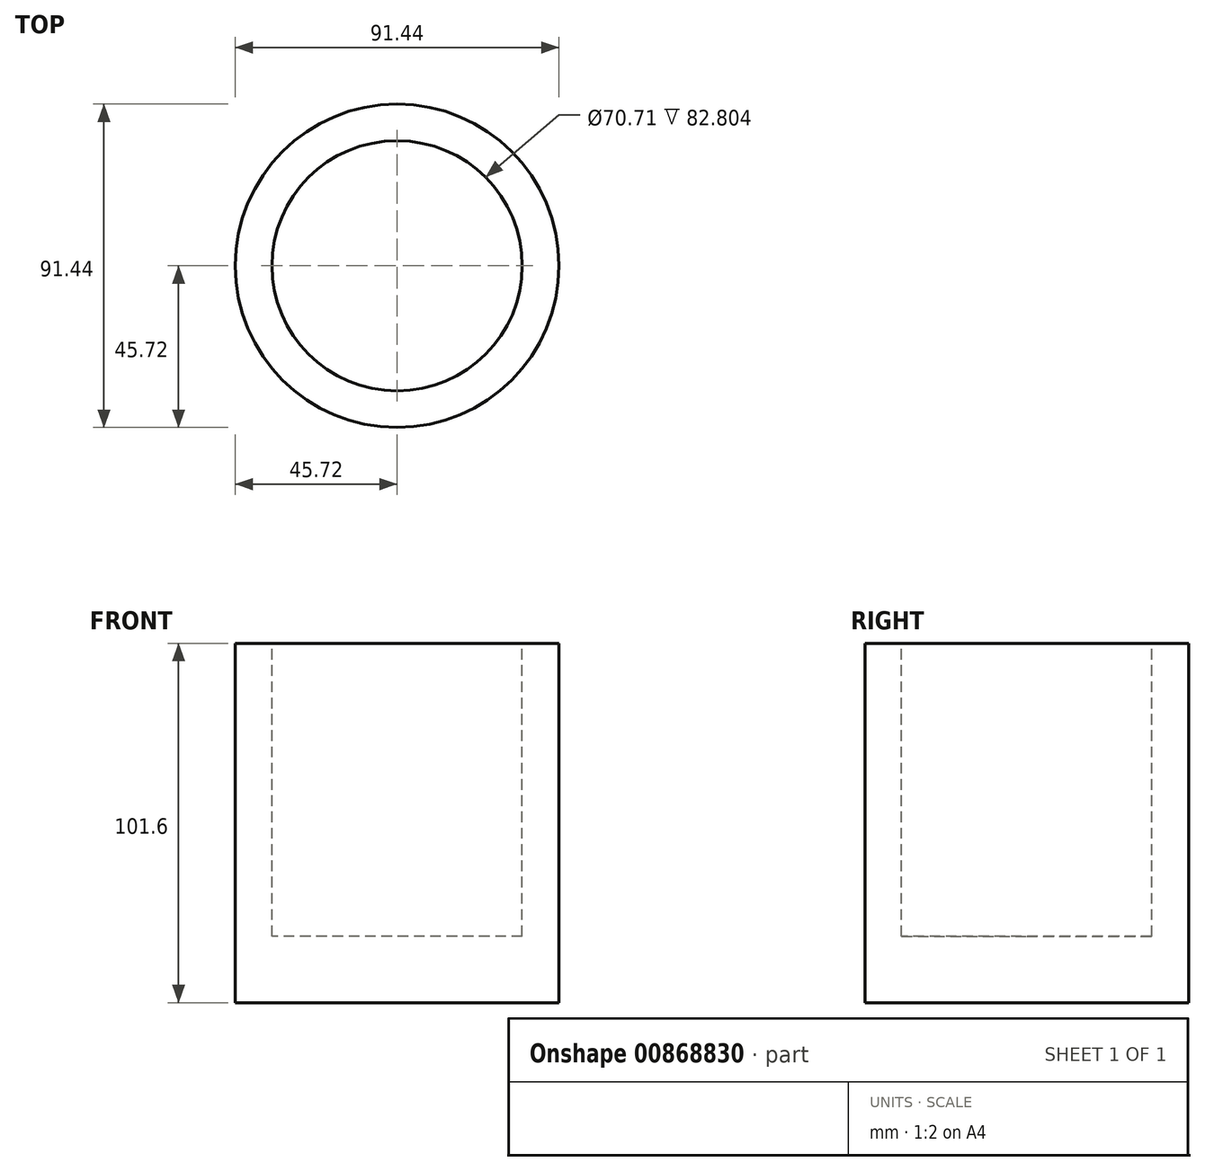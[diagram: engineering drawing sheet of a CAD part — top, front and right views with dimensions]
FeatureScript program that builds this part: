
annotation { "Feature Type Name" : "Feature", "Feature Type Description" : "" }
export const myFeature = defineFeature(function(context is Context, id is Id, definition is map)
    precondition{}
    {
        {
            var Q0;
            Q0=qCreatedBy(makeId("Top.planeOp"),FACE);
            var sketch = newSketch(context, id + "F0", { "sketchPlane" : qUnion([Q0])});
            skCircle(sketch, "E0", {"center": v(0, 0) * mm, "radius": 45.72 * mm});
            skPoint(sketch, "E0.first.point", {"position": v(-32.88, 31.77) * mm});
            skPoint(sketch, "E0.second.point", {"position": v(32.45, -32.21) * mm});
            skPoint(sketch, "E0.third.point", {"position": v(21.79, 40.2) * mm});
            skSolve(sketch);
        }
        {
            var Q0;
            Q0=makeQuery(id+"F0.imprint","IMPRINT",FACE,{"disambiguationData":[TD([[makeQuery(id+"F0.imprint","IMPRINT",EDGE,{"derivedFrom":sQuery(id+"F0.wireOp",EDGE,"E0")}),1.0]])]});
            extrude(context, id + "F1", {"entities" : qUnion([Q0]), "depth" : 101.6 * mm, "offsetDistance" : 25.4 * mm});
        }
        {
            var Q0;
            Q0=makeQuery(id+"F1.opExtrude","CAP_FACE",FACE,{"disambiguationData":[OSD([sQuery(id+"F0.wireOp",EDGE,"E0")])],"isStart":false});
            var sketch = newSketch(context, id + "F2", { "sketchPlane" : qUnion([Q0])});
            skCircle(sketch, "E1", {"center": v(0, 0) * mm, "radius": 35.35 * mm});
            skSolve(sketch);
        }
        {
            var Q0;
            Q0=makeQuery(id+"F2.imprint","IMPRINT",FACE,{"disambiguationData":[TD([[makeQuery(id+"F2.imprint","IMPRINT",EDGE,{"derivedFrom":sQuery(id+"F2.wireOp",EDGE,"E1")}),1.0]])]});
            extrude(context, id + "F3", {"entities" : qUnion([Q0]), "operationType" : NewBodyOperationType.REMOVE, "oppositeDirection" : true, "depth" : 82.8 * mm, "offsetDistance" : 25.4 * mm});
        }
    });
